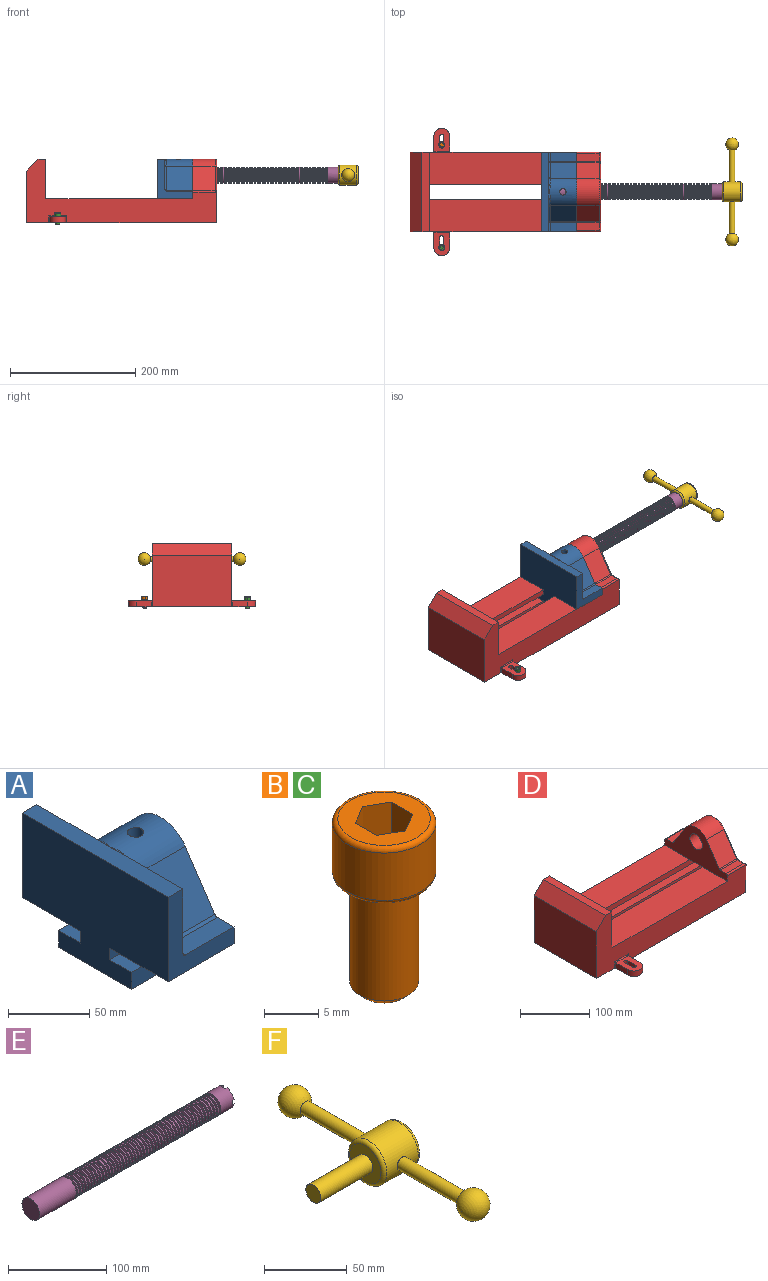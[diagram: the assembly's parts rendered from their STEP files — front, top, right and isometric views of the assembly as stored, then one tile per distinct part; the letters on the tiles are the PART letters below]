
ASSEMBLY  parts=6 mates=6
PART A: 36 faces, bbox 57.2x127x89 mm
  f0: plane 57.15x50.8mm, normal (0,0,-1), area 2903.2mm2, adj f6,f9,f10,f23
  f1: cylinder r=12.7mm len=44.45mm, axis (1,0,0), area 3464.3mm2, adj f6,f15,f16
  f2: plane 41.91x14.52mm, normal (0,0,1), area 608.5mm2, adj f6,f11,f24,f25
  f3: plane 51.86x48.26mm, normal (1,0,0), area 1495.7mm2, adj f8,f10,f31,f33,f35
  f4: plane 51.86x48.26mm, normal (1,0,0), area 1495.7mm2, adj f8,f11,f24,f28,f29
  f5: plane 57.15x50.8mm, normal (0,0,-1), area 2903.2mm2, adj f6,f9,f11,f22
  f6: plane 127x85.09mm, normal (1,0,0), area 5190.6mm2, adj f0,f1,f2,f5,f7,f10,f11,f12
  f7: plane 41.91x14.52mm, normal (0,0,1), area 608.5mm2, adj f6,f10,f30,f31
  f8: plane 127x12.7mm, normal (0,0,1), area 1612.9mm2, adj f3,f4,f9,f10,f11,f26,f34
  f9: plane 127x85.09mm, normal (-1,0,0), area 9096.8mm2, adj f0,f5,f8,f10,f11,f17,f18,f19
  f10: plane 63.5x57.15mm, normal (0,-1,0), area 1372.3mm2, adj f0,f3,f6,f7,f8,f9,f31
  f11: plane 63.5x57.15mm, normal (0,1,0), area 1372.3mm2, adj f2,f4,f5,f6,f8,f9,f24
  f12: plane 41.91x38.43mm, normal (0,-0.83,0.56), area 1939.2mm2, adj f6,f13,f30,f33
  f13: cylinder r=25.4mm len=44.45mm, axis (1,0,0), area 2026.5mm2, adj f6,f12,f14,f16,f26,f28,f34,f35
  f14: plane 41.91x38.43mm, normal (0,0.83,0.56), area 1939.2mm2, adj f6,f13,f25,f29
  f15: plane 25.4x25.4mm, normal (1,0,0), area 506.7mm2, adj f1
  f16: cylinder r=5.08mm len=13.76mm, axis (0,0,1), area 414mm2, adj f1,f13
  f17: plane 57.15x19.05mm, normal (0,0,1), area 1088.7mm2, adj f6,f9,f18,f23
  f18: plane 57.15x12.7mm, normal (0,-1,0), area 725.8mm2, adj f6,f9,f17,f19
  f19: plane 63.5x57.15mm, normal (0,0,-1), area 3629mm2, adj f6,f9,f18,f20
  f20: plane 57.15x12.7mm, normal (0,1,0), area 725.8mm2, adj f6,f9,f19,f21
  f21: plane 57.15x19.05mm, normal (0,0,1), area 1088.7mm2, adj f6,f9,f20,f22
  f22: plane 57.15x8.89mm, normal (0,1,0), area 508.1mm2, adj f5,f6,f9,f21
  f23: plane 57.15x8.89mm, normal (0,-1,0), area 508.1mm2, adj f0,f6,f9,f17
  f24: cylinder r=2.54mm len=14.52mm, axis (0,-1,0), area 57.9mm2, adj f2,f4,f11,f27
  f25: cylinder r=2.54mm len=41.91mm, axis (1,0,0), area 104.3mm2, adj f2,f6,f14,f27
  f26: bspline ~12.24x2.8mm, area 20.9mm2, adj f8,f13,f28
  f27: sphere r=2.54mm, area 6.3mm2, adj f24,f25,f29
  f28: torus R=27.94mm, axis (1,0,0), area 57.8mm2, adj f4,f13,f26,f29
  f29: cylinder r=2.54mm len=39.84mm, axis (0,-0.56,0.83), area 184.6mm2, adj f4,f14,f27,f28
  f30: cylinder r=2.54mm len=41.91mm, axis (1,0,0), area 104.3mm2, adj f6,f7,f12,f32
  f31: cylinder r=2.54mm len=14.52mm, axis (0,-1,0), area 57.9mm2, adj f3,f7,f10,f32
  f32: sphere r=2.54mm, area 6.3mm2, adj f30,f31,f33
  f33: cylinder r=2.54mm len=39.84mm, axis (0,-0.56,-0.83), area 184.6mm2, adj f3,f12,f32,f35
  f34: bspline ~12.24x2.8mm, area 20.9mm2, adj f8,f13,f35
  f35: torus R=27.94mm, axis (1,0,0), area 57.8mm2, adj f3,f13,f33,f34
PART B: 15 faces, bbox 10.3x10.3x19.1 mm
  f0: plane 8.51x8.51mm, normal (0,0,1), area 37.2mm2, adj f5,f6,f7,f8,f9,f10,f14
  f1: cylinder r=3.17mm len=11.94mm, axis (0,0,1), area 238.2mm2, adj f4,f12
  f2: plane 4.83x4.83mm, normal (0,0,-1), area 18.3mm2, adj f12
  f3: cylinder r=4.76mm len=9.53mm, axis (0,0,-1), area 159.6mm2, adj f13,f14
  f4: plane 8.51x8.51mm, normal (0,0,-1), area 25.2mm2, adj f1,f13
  f5: plane 4.83x2.38mm, normal (-0.5,-0.87,0), area 13.3mm2, adj f0,f6,f10,f11
  f6: plane 4.83x2.38mm, normal (0.5,-0.87,0), area 13.3mm2, adj f0,f5,f7,f11
  f7: plane 4.83x2.75mm, normal (1,0,0), area 13.3mm2, adj f0,f6,f8,f11
  f8: plane 4.83x2.38mm, normal (0.5,0.87,0), area 13.3mm2, adj f0,f7,f9,f11
  f9: plane 4.83x2.38mm, normal (-0.5,0.87,0), area 13.3mm2, adj f0,f8,f10,f11
  f10: plane 4.83x2.75mm, normal (-1,0,0), area 13.3mm2, adj f0,f5,f9,f11
  f11: plane 5.5x4.76mm, normal (0,0,1), area 19.6mm2, adj f5,f6,f7,f8,f9,f10
  f12: cone r=3.17mm half-angle=45deg, axis (0,0,1), area 18.9mm2, adj f1,f2
  f13: torus R=4.25mm, axis (0,0,1), area 23mm2, adj f3,f4
  f14: torus R=4.25mm, axis (0,0,1), area 23mm2, adj f0,f3
PART C: same geometry as B
PART D: 61 faces, bbox 304.8x203.2x103.7 mm
  f0: plane 304.8x101.6mm, normal (0,1,0), area 13520.3mm2, adj f3,f4,f5,f6,f7,f8,f9,f16
  f1: plane 304.8x101.6mm, normal (0,-1,0), area 13520.3mm2, adj f2,f3,f5,f6,f7,f8,f9,f16
  f2: plane 234.95x50.8mm, normal (0,0,1), area 11935.5mm2, adj f1,f5,f16,f26
  f3: plane 127x99.06mm, normal (1,0,0), area 7097.5mm2, adj f0,f1,f9,f14,f17,f18,f19,f20
  f4: plane 234.95x50.8mm, normal (0,0,1), area 11935.5mm2, adj f0,f5,f16,f27
  f5: plane 127x101.6mm, normal (1,0,0), area 9516.1mm2, adj f0,f1,f2,f4,f6,f9,f18,f19
  f6: plane 127x12.7mm, normal (0,0,1), area 1612.9mm2, adj f0,f1,f5,f7
  f7: plane 127x19.05mm, normal (-0.71,0,0.71), area 3421.5mm2, adj f0,f1,f6,f8
  f8: plane 127x82.55mm, normal (-1,0,0), area 10483.8mm2, adj f0,f1,f7,f9
  f9: plane 304.8x203.2mm, normal (0,0,-1), area 33298.3mm2, adj f0,f1,f3,f5,f8,f21,f22,f39
  f10: plane 35.56x11.98mm, normal (0,0,1), area 426mm2, adj f16,f28,f29,f30
  f11: plane 38.43x35.56mm, normal (0,0.83,0.56), area 1645.4mm2, adj f12,f16,f29,f32
  f12: cylinder r=25.4mm len=42.19mm, axis (1,0,0), area 1770.2mm2, adj f11,f13,f16,f33
  f13: plane 38.43x35.56mm, normal (0,-0.83,0.56), area 1645.4mm2, adj f12,f16,f34,f35
  f14: cylinder r=12.7mm len=38.1mm, axis (1,0,0), area 3040.2mm2, adj f3,f16
  f15: plane 35.56x11.98mm, normal (0,0,1), area 426mm2, adj f16,f34,f36,f38
  f16: plane 127x63.5mm, normal (-1,0,0), area 4155.5mm2, adj f0,f1,f2,f4,f10,f11,f12,f13
  f17: plane 38.1x25.4mm, normal (0,0,-1), area 967.7mm2, adj f3,f16,f26,f27
  f18: plane 273.05x19.05mm, normal (0,0,-1), area 5201.6mm2, adj f3,f5,f19,f26
  f19: plane 273.05x12.7mm, normal (0,1,0), area 3467.7mm2, adj f3,f5,f18,f20
  f20: plane 273.05x19.05mm, normal (0,0,1), area 5201.6mm2, adj f3,f5,f19,f21
  f21: plane 273.05x16.51mm, normal (0,1,0), area 4508.1mm2, adj f3,f5,f9,f20
  f22: plane 273.05x16.51mm, normal (0,-1,0), area 4508.1mm2, adj f3,f5,f9,f23
  f23: plane 273.05x19.05mm, normal (0,0,1), area 5201.6mm2, adj f3,f5,f22,f24
  f24: plane 273.05x12.7mm, normal (0,-1,0), area 3467.7mm2, adj f3,f5,f23,f25
  f25: plane 273.05x19.05mm, normal (0,0,-1), area 5201.6mm2, adj f3,f5,f24,f27
  f26: plane 273.05x8.89mm, normal (0,1,0), area 2427.4mm2, adj f2,f3,f5,f17,f18
  f27: plane 273.05x8.89mm, normal (0,-1,0), area 2427.4mm2, adj f3,f4,f5,f17,f25
  f28: cylinder r=2.54mm len=38.1mm, axis (1,0,0), area 148.3mm2, adj f0,f10,f16,f30
  f29: cylinder r=2.54mm len=35.56mm, axis (-1,0,0), area 88.5mm2, adj f10,f11,f16,f31
  f30: cylinder r=2.54mm len=14.52mm, axis (0,1,0), area 54.3mm2, adj f3,f10,f28,f31
  f31: torus R=5.08mm, axis (-1,0,0), area 13.5mm2, adj f3,f29,f30,f32
  f32: cylinder r=2.54mm len=39.84mm, axis (0,0.56,-0.83), area 184.6mm2, adj f3,f11,f31,f33
  f33: torus R=22.86mm, axis (-1,0,0), area 191.4mm2, adj f3,f12,f32,f35
  f34: cylinder r=2.54mm len=35.56mm, axis (-1,0,0), area 88.5mm2, adj f13,f15,f16,f37
  f35: cylinder r=2.54mm len=39.84mm, axis (0,0.56,0.83), area 184.6mm2, adj f3,f13,f33,f37
  f36: cylinder r=2.54mm len=38.1mm, axis (-1,0,0), area 148.3mm2, adj f1,f15,f16,f38
  f37: torus R=5.08mm, axis (-1,0,0), area 13.5mm2, adj f3,f34,f35,f38
  f38: cylinder r=2.54mm len=14.52mm, axis (0,1,0), area 54.3mm2, adj f3,f15,f36,f37
  f39: plane 23.88x9.53mm, normal (-1,0,0), area 227.4mm2, adj f9,f45,f46,f60
  f40: plane 23.88x9.53mm, normal (1,0,0), area 227.4mm2, adj f9,f45,f46,f58
  f41: cylinder r=3.3mm len=9.53mm, axis (0,0,-1), area 98.8mm2, adj f9,f42,f44,f46
  f42: plane 15.62x9.53mm, normal (-1,0,0), area 148.8mm2, adj f9,f41,f43,f46
  f43: cylinder r=3.3mm len=9.53mm, axis (0,0,-1), area 98.8mm2, adj f9,f42,f44,f46
  f44: plane 15.62x9.53mm, normal (1,0,0), area 148.8mm2, adj f9,f41,f43,f46
  f45: cylinder r=12.7mm len=25.4mm, axis (0,0,-1), area 380mm2, adj f9,f39,f40,f46
  f46: plane 36.58x25.4mm, normal (0,0,1), area 722.4mm2, adj f39,f40,f41,f42,f43,f44,f45,f59
  f47: plane 23.88x9.53mm, normal (-1,0,0), area 227.4mm2, adj f9,f53,f54,f56
  f48: plane 23.88x9.53mm, normal (1,0,0), area 227.4mm2, adj f9,f53,f54,f55
  f49: cylinder r=3.3mm len=9.53mm, axis (0,0,-1), area 98.8mm2, adj f9,f50,f52,f54
  f50: plane 15.62x9.53mm, normal (-1,0,0), area 148.8mm2, adj f9,f49,f51,f54
  f51: cylinder r=3.3mm len=9.53mm, axis (0,0,-1), area 98.8mm2, adj f9,f50,f52,f54
  f52: plane 15.62x9.53mm, normal (1,0,0), area 148.8mm2, adj f9,f49,f51,f54
  f53: cylinder r=12.7mm len=25.4mm, axis (0,0,-1), area 380mm2, adj f9,f47,f48,f54
  f54: plane 36.58x25.4mm, normal (0,0,1), area 722.4mm2, adj f47,f48,f49,f50,f51,f52,f53,f57
  f55: cylinder r=1.52mm len=11.05mm, axis (0,0,-1), area 24.1mm2, adj f0,f9,f48,f57
  f56: cylinder r=1.52mm len=11.05mm, axis (0,0,1), area 24.1mm2, adj f0,f9,f47,f57
  f57: cylinder r=1.52mm len=28.45mm, axis (1,0,0), area 63.5mm2, adj f0,f54,f55,f56
  f58: cylinder r=1.52mm len=11.05mm, axis (0,0,1), area 24.1mm2, adj f1,f9,f40,f59
  f59: cylinder r=1.52mm len=28.45mm, axis (-1,0,0), area 63.5mm2, adj f1,f46,f58,f60
  f60: cylinder r=1.52mm len=11.05mm, axis (0,0,-1), area 24.1mm2, adj f1,f9,f39,f59
PART E: 220 faces, bbox 279.4x25.4x25.4 mm
  f0: cylinder r=12.7mm len=25.4mm, axis (-1,0,0), area 1468.2mm2, adj f1,f2,f3,f5,f7,f208,f209,f210
  f1: plane 9.9x9.9mm, normal (1,0,0), area 62.3mm2, adj f0,f4,f213,f216
  f2: plane 9.9x9.9mm, normal (1,0,0), area 62.3mm2, adj f0,f4,f210,f218
  f3: plane 9.9x9.9mm, normal (1,0,0), area 62.3mm2, adj f0,f4,f209,f212
  f4: cylinder r=6.35mm len=25.4mm, axis (1,0,0), area 960.3mm2, adj f1,f2,f3,f5,f6,f208,f209,f210
  f5: plane 9.9x9.9mm, normal (1,0,0), area 62.3mm2, adj f0,f4,f215,f217
  f6: plane 12.7x12.7mm, normal (1,0,0), area 126.7mm2, adj f4
  f7: cone r=12.7mm half-angle=76deg, axis (1,0,0), area 188mm2, adj f0,f9
  f8: cone r=10.16mm half-angle=76deg, axis (-1,0,0), area 188mm2, adj f9,f10
  f9: cylinder r=10.16mm len=20.32mm, axis (1,0,0), area 81.1mm2, adj f7,f8
  f10: cylinder r=12.7mm len=25.4mm, axis (-1,0,0), area 131.7mm2, adj f8,f11
  f11: cone r=12.7mm half-angle=76deg, axis (1,0,0), area 188mm2, adj f10,f13
  f12: cone r=10.16mm half-angle=76deg, axis (-1,0,0), area 188mm2, adj f13,f14
  f13: cylinder r=10.16mm len=20.32mm, axis (1,0,0), area 81.1mm2, adj f11,f12
  f14: cylinder r=12.7mm len=25.4mm, axis (-1,0,0), area 131.7mm2, adj f12,f15
  f15: cone r=12.7mm half-angle=76deg, axis (1,0,0), area 188mm2, adj f14,f17
  f16: cone r=10.16mm half-angle=76deg, axis (-1,0,0), area 188mm2, adj f17,f18
  f17: cylinder r=10.16mm len=20.32mm, axis (1,0,0), area 81.1mm2, adj f15,f16
  f18: cylinder r=12.7mm len=25.4mm, axis (-1,0,0), area 131.7mm2, adj f16,f19
  f19: cone r=12.7mm half-angle=76deg, axis (1,0,0), area 188mm2, adj f18,f21
  f20: cone r=10.16mm half-angle=76deg, axis (-1,0,0), area 188mm2, adj f21,f22
  f21: cylinder r=10.16mm len=20.32mm, axis (1,0,0), area 81.1mm2, adj f19,f20
  f22: cylinder r=12.7mm len=25.4mm, axis (-1,0,0), area 131.7mm2, adj f20,f23
  f23: cone r=12.7mm half-angle=76deg, axis (1,0,0), area 188mm2, adj f22,f25
  f24: cone r=10.16mm half-angle=76deg, axis (-1,0,0), area 188mm2, adj f25,f26
  f25: cylinder r=10.16mm len=20.32mm, axis (1,0,0), area 81.1mm2, adj f23,f24
  f26: cylinder r=12.7mm len=25.4mm, axis (-1,0,0), area 131.7mm2, adj f24,f27
  f27: cone r=12.7mm half-angle=76deg, axis (1,0,0), area 188mm2, adj f26,f29
  f28: cone r=10.16mm half-angle=76deg, axis (-1,0,0), area 188mm2, adj f29,f30
  f29: cylinder r=10.16mm len=20.32mm, axis (1,0,0), area 81.1mm2, adj f27,f28
  f30: cylinder r=12.7mm len=25.4mm, axis (-1,0,0), area 131.7mm2, adj f28,f31
  f31: cone r=12.7mm half-angle=76deg, axis (1,0,0), area 188mm2, adj f30,f33
  f32: cone r=10.16mm half-angle=76deg, axis (-1,0,0), area 188mm2, adj f33,f34
  f33: cylinder r=10.16mm len=20.32mm, axis (1,0,0), area 81.1mm2, adj f31,f32
  f34: cylinder r=12.7mm len=25.4mm, axis (-1,0,0), area 131.7mm2, adj f32,f35
  f35: cone r=12.7mm half-angle=76deg, axis (1,0,0), area 188mm2, adj f34,f37
  f36: cone r=10.16mm half-angle=76deg, axis (-1,0,0), area 188mm2, adj f37,f38
  f37: cylinder r=10.16mm len=20.32mm, axis (1,0,0), area 81.1mm2, adj f35,f36
  f38: cylinder r=12.7mm len=25.4mm, axis (-1,0,0), area 131.7mm2, adj f36,f39
  f39: cone r=12.7mm half-angle=76deg, axis (1,0,0), area 188mm2, adj f38,f41
  f40: cone r=10.16mm half-angle=76deg, axis (-1,0,0), area 188mm2, adj f41,f42
  f41: cylinder r=10.16mm len=20.32mm, axis (1,0,0), area 81.1mm2, adj f39,f40
  f42: cylinder r=12.7mm len=25.4mm, axis (-1,0,0), area 131.7mm2, adj f40,f43
  f43: cone r=12.7mm half-angle=76deg, axis (1,0,0), area 188mm2, adj f42,f45
  f44: cone r=10.16mm half-angle=76deg, axis (-1,0,0), area 188mm2, adj f45,f46
  f45: cylinder r=10.16mm len=20.32mm, axis (1,0,0), area 81.1mm2, adj f43,f44
  f46: cylinder r=12.7mm len=25.4mm, axis (-1,0,0), area 131.7mm2, adj f44,f47
  f47: cone r=12.7mm half-angle=76deg, axis (1,0,0), area 188mm2, adj f46,f49
  f48: cone r=10.16mm half-angle=76deg, axis (-1,0,0), area 188mm2, adj f49,f50
  f49: cylinder r=10.16mm len=20.32mm, axis (1,0,0), area 81.1mm2, adj f47,f48
  f50: cylinder r=12.7mm len=25.4mm, axis (-1,0,0), area 131.7mm2, adj f48,f51
  f51: cone r=12.7mm half-angle=76deg, axis (1,0,0), area 188mm2, adj f50,f53
  f52: cone r=10.16mm half-angle=76deg, axis (-1,0,0), area 188mm2, adj f53,f54
  f53: cylinder r=10.16mm len=20.32mm, axis (1,0,0), area 81.1mm2, adj f51,f52
  f54: cylinder r=12.7mm len=25.4mm, axis (-1,0,0), area 131.7mm2, adj f52,f55
  f55: cone r=12.7mm half-angle=76deg, axis (1,0,0), area 188mm2, adj f54,f57
  f56: cone r=10.16mm half-angle=76deg, axis (-1,0,0), area 188mm2, adj f57,f58
  f57: cylinder r=10.16mm len=20.32mm, axis (1,0,0), area 81.1mm2, adj f55,f56
  f58: cylinder r=12.7mm len=25.4mm, axis (-1,0,0), area 131.7mm2, adj f56,f59
  f59: cone r=12.7mm half-angle=76deg, axis (1,0,0), area 188mm2, adj f58,f61
  f60: cone r=10.16mm half-angle=76deg, axis (-1,0,0), area 188mm2, adj f61,f62
  f61: cylinder r=10.16mm len=20.32mm, axis (1,0,0), area 81.1mm2, adj f59,f60
  f62: cylinder r=12.7mm len=25.4mm, axis (-1,0,0), area 131.7mm2, adj f60,f63
  f63: cone r=12.7mm half-angle=76deg, axis (1,0,0), area 188mm2, adj f62,f65
  f64: cone r=10.16mm half-angle=76deg, axis (-1,0,0), area 188mm2, adj f65,f66
  f65: cylinder r=10.16mm len=20.32mm, axis (1,0,0), area 81.1mm2, adj f63,f64
  f66: cylinder r=12.7mm len=25.4mm, axis (-1,0,0), area 131.7mm2, adj f64,f67
  f67: cone r=12.7mm half-angle=76deg, axis (1,0,0), area 188mm2, adj f66,f69
  f68: cone r=10.16mm half-angle=76deg, axis (-1,0,0), area 188mm2, adj f69,f70
  f69: cylinder r=10.16mm len=20.32mm, axis (1,0,0), area 81.1mm2, adj f67,f68
  f70: cylinder r=12.7mm len=25.4mm, axis (-1,0,0), area 131.7mm2, adj f68,f71
  f71: cone r=12.7mm half-angle=76deg, axis (1,0,0), area 188mm2, adj f70,f73
  f72: cone r=10.16mm half-angle=76deg, axis (-1,0,0), area 188mm2, adj f73,f74
  f73: cylinder r=10.16mm len=20.32mm, axis (1,0,0), area 81.1mm2, adj f71,f72
  f74: cylinder r=12.7mm len=25.4mm, axis (-1,0,0), area 131.7mm2, adj f72,f75
  f75: cone r=12.7mm half-angle=76deg, axis (1,0,0), area 188mm2, adj f74,f77
  f76: cone r=10.16mm half-angle=76deg, axis (-1,0,0), area 188mm2, adj f77,f78
  f77: cylinder r=10.16mm len=20.32mm, axis (1,0,0), area 81.1mm2, adj f75,f76
  f78: cylinder r=12.7mm len=25.4mm, axis (-1,0,0), area 131.7mm2, adj f76,f79
  f79: cone r=12.7mm half-angle=76deg, axis (1,0,0), area 188mm2, adj f78,f81
  f80: cone r=10.16mm half-angle=76deg, axis (-1,0,0), area 188mm2, adj f81,f82
  f81: cylinder r=10.16mm len=20.32mm, axis (1,0,0), area 81.1mm2, adj f79,f80
  f82: cylinder r=12.7mm len=25.4mm, axis (-1,0,0), area 131.7mm2, adj f80,f83
  f83: cone r=12.7mm half-angle=76deg, axis (1,0,0), area 188mm2, adj f82,f85
  f84: cone r=10.16mm half-angle=76deg, axis (-1,0,0), area 188mm2, adj f85,f86
  f85: cylinder r=10.16mm len=20.32mm, axis (1,0,0), area 81.1mm2, adj f83,f84
  f86: cylinder r=12.7mm len=25.4mm, axis (-1,0,0), area 131.7mm2, adj f84,f87
  f87: cone r=12.7mm half-angle=76deg, axis (1,0,0), area 188mm2, adj f86,f89
  f88: cone r=10.16mm half-angle=76deg, axis (-1,0,0), area 188mm2, adj f89,f90
  f89: cylinder r=10.16mm len=20.32mm, axis (1,0,0), area 81.1mm2, adj f87,f88
  f90: cylinder r=12.7mm len=25.4mm, axis (-1,0,0), area 131.7mm2, adj f88,f91
  f91: cone r=12.7mm half-angle=76deg, axis (1,0,0), area 188mm2, adj f90,f93
  f92: cone r=10.16mm half-angle=76deg, axis (-1,0,0), area 188mm2, adj f93,f94
  f93: cylinder r=10.16mm len=20.32mm, axis (1,0,0), area 81.1mm2, adj f91,f92
  f94: cylinder r=12.7mm len=25.4mm, axis (-1,0,0), area 131.7mm2, adj f92,f95
  f95: cone r=12.7mm half-angle=76deg, axis (1,0,0), area 188mm2, adj f94,f97
  f96: cone r=10.16mm half-angle=76deg, axis (-1,0,0), area 188mm2, adj f97,f98
  f97: cylinder r=10.16mm len=20.32mm, axis (1,0,0), area 81.1mm2, adj f95,f96
  f98: cylinder r=12.7mm len=25.4mm, axis (-1,0,0), area 131.7mm2, adj f96,f99
  f99: cone r=12.7mm half-angle=76deg, axis (1,0,0), area 188mm2, adj f98,f101
  f100: cone r=10.16mm half-angle=76deg, axis (-1,0,0), area 188mm2, adj f101,f102
  f101: cylinder r=10.16mm len=20.32mm, axis (1,0,0), area 81.1mm2, adj f99,f100
  f102: cylinder r=12.7mm len=25.4mm, axis (-1,0,0), area 131.7mm2, adj f100,f103
  f103: cone r=12.7mm half-angle=76deg, axis (1,0,0), area 188mm2, adj f102,f105
  f104: cone r=10.16mm half-angle=76deg, axis (-1,0,0), area 188mm2, adj f105,f106
  f105: cylinder r=10.16mm len=20.32mm, axis (1,0,0), area 81.1mm2, adj f103,f104
  f106: cylinder r=12.7mm len=25.4mm, axis (-1,0,0), area 131.7mm2, adj f104,f107
  f107: cone r=12.7mm half-angle=76deg, axis (1,0,0), area 188mm2, adj f106,f109
  f108: cone r=10.16mm half-angle=76deg, axis (-1,0,0), area 188mm2, adj f109,f110
  f109: cylinder r=10.16mm len=20.32mm, axis (1,0,0), area 81.1mm2, adj f107,f108
  f110: cylinder r=12.7mm len=25.4mm, axis (-1,0,0), area 131.7mm2, adj f108,f111
  f111: cone r=12.7mm half-angle=76deg, axis (1,0,0), area 188mm2, adj f110,f113
  f112: cone r=10.16mm half-angle=76deg, axis (-1,0,0), area 188mm2, adj f113,f114
  f113: cylinder r=10.16mm len=20.32mm, axis (1,0,0), area 81.1mm2, adj f111,f112
  f114: cylinder r=12.7mm len=25.4mm, axis (-1,0,0), area 131.7mm2, adj f112,f115
  f115: cone r=12.7mm half-angle=76deg, axis (1,0,0), area 188mm2, adj f114,f117
  f116: cone r=10.16mm half-angle=76deg, axis (-1,0,0), area 188mm2, adj f117,f118
  f117: cylinder r=10.16mm len=20.32mm, axis (1,0,0), area 81.1mm2, adj f115,f116
  f118: cylinder r=12.7mm len=25.4mm, axis (-1,0,0), area 131.7mm2, adj f116,f119
  f119: cone r=12.7mm half-angle=76deg, axis (1,0,0), area 188mm2, adj f118,f121
  f120: cone r=10.16mm half-angle=76deg, axis (-1,0,0), area 188mm2, adj f121,f122
  f121: cylinder r=10.16mm len=20.32mm, axis (1,0,0), area 81.1mm2, adj f119,f120
  f122: cylinder r=12.7mm len=25.4mm, axis (-1,0,0), area 131.7mm2, adj f120,f123
  f123: cone r=12.7mm half-angle=76deg, axis (1,0,0), area 188mm2, adj f122,f125
  f124: cone r=10.16mm half-angle=76deg, axis (-1,0,0), area 188mm2, adj f125,f126
  f125: cylinder r=10.16mm len=20.32mm, axis (1,0,0), area 81.1mm2, adj f123,f124
  f126: cylinder r=12.7mm len=25.4mm, axis (-1,0,0), area 131.7mm2, adj f124,f127
  f127: cone r=12.7mm half-angle=76deg, axis (1,0,0), area 188mm2, adj f126,f129
  f128: cone r=10.16mm half-angle=76deg, axis (-1,0,0), area 188mm2, adj f129,f130
  f129: cylinder r=10.16mm len=20.32mm, axis (1,0,0), area 81.1mm2, adj f127,f128
  f130: cylinder r=12.7mm len=25.4mm, axis (-1,0,0), area 131.7mm2, adj f128,f131
  f131: cone r=12.7mm half-angle=76deg, axis (1,0,0), area 188mm2, adj f130,f133
  f132: cone r=10.16mm half-angle=76deg, axis (-1,0,0), area 188mm2, adj f133,f134
  f133: cylinder r=10.16mm len=20.32mm, axis (1,0,0), area 81.1mm2, adj f131,f132
  f134: cylinder r=12.7mm len=25.4mm, axis (-1,0,0), area 131.7mm2, adj f132,f135
  f135: cone r=12.7mm half-angle=76deg, axis (1,0,0), area 188mm2, adj f134,f137
  f136: cone r=10.16mm half-angle=76deg, axis (-1,0,0), area 188mm2, adj f137,f138
  f137: cylinder r=10.16mm len=20.32mm, axis (1,0,0), area 81.1mm2, adj f135,f136
  f138: cylinder r=12.7mm len=25.4mm, axis (-1,0,0), area 131.7mm2, adj f136,f139
  f139: cone r=12.7mm half-angle=76deg, axis (1,0,0), area 188mm2, adj f138,f141
  f140: cone r=10.16mm half-angle=76deg, axis (-1,0,0), area 188mm2, adj f141,f142
  f141: cylinder r=10.16mm len=20.32mm, axis (1,0,0), area 81.1mm2, adj f139,f140
  f142: cylinder r=12.7mm len=25.4mm, axis (-1,0,0), area 131.7mm2, adj f140,f143
  f143: cone r=12.7mm half-angle=76deg, axis (1,0,0), area 188mm2, adj f142,f145
  f144: cone r=10.16mm half-angle=76deg, axis (-1,0,0), area 188mm2, adj f145,f146
  f145: cylinder r=10.16mm len=20.32mm, axis (1,0,0), area 81.1mm2, adj f143,f144
  f146: cylinder r=12.7mm len=25.4mm, axis (-1,0,0), area 131.7mm2, adj f144,f147
  f147: cone r=12.7mm half-angle=76deg, axis (1,0,0), area 188mm2, adj f146,f149
  f148: cone r=10.16mm half-angle=76deg, axis (-1,0,0), area 188mm2, adj f149,f150
  f149: cylinder r=10.16mm len=20.32mm, axis (1,0,0), area 81.1mm2, adj f147,f148
  f150: cylinder r=12.7mm len=25.4mm, axis (-1,0,0), area 131.7mm2, adj f148,f151
  f151: cone r=12.7mm half-angle=76deg, axis (1,0,0), area 188mm2, adj f150,f153
  f152: cone r=10.16mm half-angle=76deg, axis (-1,0,0), area 188mm2, adj f153,f154
  f153: cylinder r=10.16mm len=20.32mm, axis (1,0,0), area 81.1mm2, adj f151,f152
  f154: cylinder r=12.7mm len=25.4mm, axis (-1,0,0), area 131.7mm2, adj f152,f155
  f155: cone r=12.7mm half-angle=76deg, axis (1,0,0), area 188mm2, adj f154,f157
  f156: cone r=10.16mm half-angle=76deg, axis (-1,0,0), area 188mm2, adj f157,f158
  f157: cylinder r=10.16mm len=20.32mm, axis (1,0,0), area 81.1mm2, adj f155,f156
  f158: cylinder r=12.7mm len=25.4mm, axis (-1,0,0), area 131.7mm2, adj f156,f159
  f159: cone r=12.7mm half-angle=76deg, axis (1,0,0), area 188mm2, adj f158,f161
  f160: cone r=10.16mm half-angle=76deg, axis (-1,0,0), area 188mm2, adj f161,f162
  f161: cylinder r=10.16mm len=20.32mm, axis (1,0,0), area 81.1mm2, adj f159,f160
  f162: cylinder r=12.7mm len=25.4mm, axis (-1,0,0), area 131.7mm2, adj f160,f163
  f163: cone r=12.7mm half-angle=76deg, axis (1,0,0), area 188mm2, adj f162,f165
  f164: cone r=10.16mm half-angle=76deg, axis (-1,0,0), area 188mm2, adj f165,f166
  f165: cylinder r=10.16mm len=20.32mm, axis (1,0,0), area 81.1mm2, adj f163,f164
  f166: cylinder r=12.7mm len=25.4mm, axis (-1,0,0), area 131.7mm2, adj f164,f167
  f167: cone r=12.7mm half-angle=76deg, axis (1,0,0), area 188mm2, adj f166,f169
  f168: cone r=10.16mm half-angle=76deg, axis (-1,0,0), area 188mm2, adj f169,f170
  f169: cylinder r=10.16mm len=20.32mm, axis (1,0,0), area 81.1mm2, adj f167,f168
  f170: cylinder r=12.7mm len=25.4mm, axis (-1,0,0), area 131.7mm2, adj f168,f171
  f171: cone r=12.7mm half-angle=76deg, axis (1,0,0), area 188mm2, adj f170,f173
  f172: cone r=10.16mm half-angle=76deg, axis (-1,0,0), area 188mm2, adj f173,f174
  f173: cylinder r=10.16mm len=20.32mm, axis (1,0,0), area 81.1mm2, adj f171,f172
  f174: cylinder r=12.7mm len=25.4mm, axis (-1,0,0), area 131.7mm2, adj f172,f175
  f175: cone r=12.7mm half-angle=76deg, axis (1,0,0), area 188mm2, adj f174,f177
  f176: cone r=10.16mm half-angle=76deg, axis (-1,0,0), area 188mm2, adj f177,f178
  f177: cylinder r=10.16mm len=20.32mm, axis (1,0,0), area 81.1mm2, adj f175,f176
  f178: cylinder r=12.7mm len=25.4mm, axis (-1,0,0), area 131.7mm2, adj f176,f179
  f179: cone r=12.7mm half-angle=76deg, axis (1,0,0), area 188mm2, adj f178,f181
  f180: cone r=10.16mm half-angle=76deg, axis (-1,0,0), area 188mm2, adj f181,f182
  f181: cylinder r=10.16mm len=20.32mm, axis (1,0,0), area 81.1mm2, adj f179,f180
  f182: cylinder r=12.7mm len=25.4mm, axis (-1,0,0), area 131.7mm2, adj f180,f183
  f183: cone r=12.7mm half-angle=76deg, axis (1,0,0), area 188mm2, adj f182,f185
  f184: cone r=10.16mm half-angle=76deg, axis (-1,0,0), area 188mm2, adj f185,f186
  f185: cylinder r=10.16mm len=20.32mm, axis (1,0,0), area 81.1mm2, adj f183,f184
  f186: cylinder r=12.7mm len=25.4mm, axis (-1,0,0), area 131.7mm2, adj f184,f187
  f187: cone r=12.7mm half-angle=76deg, axis (1,0,0), area 188mm2, adj f186,f189
  f188: cone r=10.16mm half-angle=76deg, axis (-1,0,0), area 188mm2, adj f189,f190
  f189: cylinder r=10.16mm len=20.32mm, axis (1,0,0), area 81.1mm2, adj f187,f188
  f190: cylinder r=12.7mm len=25.4mm, axis (-1,0,0), area 131.7mm2, adj f188,f191
  f191: cone r=12.7mm half-angle=76deg, axis (1,0,0), area 188mm2, adj f190,f193
  f192: cone r=10.16mm half-angle=76deg, axis (-1,0,0), area 188mm2, adj f193,f194
  f193: cylinder r=10.16mm len=20.32mm, axis (1,0,0), area 81.1mm2, adj f191,f192
  f194: cylinder r=12.7mm len=25.4mm, axis (-1,0,0), area 131.7mm2, adj f192,f195
  f195: cone r=12.7mm half-angle=76deg, axis (1,0,0), area 188mm2, adj f194,f197
  f196: cone r=10.16mm half-angle=76deg, axis (-1,0,0), area 188mm2, adj f197,f198
  f197: cylinder r=10.16mm len=20.32mm, axis (1,0,0), area 81.1mm2, adj f195,f196
  f198: cylinder r=12.7mm len=25.4mm, axis (-1,0,0), area 131.7mm2, adj f196,f199
  f199: cone r=12.7mm half-angle=76deg, axis (1,0,0), area 188mm2, adj f198,f201
  f200: cone r=10.16mm half-angle=76deg, axis (-1,0,0), area 188mm2, adj f201,f202
  f201: cylinder r=10.16mm len=20.32mm, axis (1,0,0), area 81.1mm2, adj f199,f200
  f202: cylinder r=12.7mm len=25.4mm, axis (-1,0,0), area 131.7mm2, adj f200,f203
  f203: cone r=12.7mm half-angle=76deg, axis (1,0,0), area 188mm2, adj f202,f205
  f204: cone r=10.16mm half-angle=76deg, axis (-1,0,0), area 188mm2, adj f205,f207
  f205: cylinder r=10.16mm len=20.32mm, axis (1,0,0), area 81.1mm2, adj f203,f204
  f206: plane 25.4x25.4mm, normal (-1,0,0), area 506.7mm2, adj f207
  f207: cylinder r=12.7mm len=52.45mm, axis (-1,0,0), area 4185.4mm2, adj f204,f206
  f208: plane 6.88x5.08mm, normal (1,0,0), area 32.7mm2, adj f0,f4,f209,f210
  f209: plane 6.62x2.54mm, normal (0,-1,0), area 16.8mm2, adj f0,f3,f4,f208
  f210: plane 6.62x2.54mm, normal (0,1,0), area 16.8mm2, adj f0,f2,f4,f208
  f211: plane 6.88x5.08mm, normal (1,0,0), area 32.7mm2, adj f0,f4,f212,f213
  f212: plane 6.62x2.54mm, normal (0,0,1), area 16.8mm2, adj f0,f3,f4,f211
  f213: plane 6.62x2.54mm, normal (0,0,-1), area 16.8mm2, adj f0,f1,f4,f211
  f214: plane 6.88x5.08mm, normal (1,0,0), area 32.7mm2, adj f0,f4,f215,f216
  f215: plane 6.62x2.54mm, normal (0,1,0), area 16.8mm2, adj f0,f4,f5,f214
  f216: plane 6.62x2.54mm, normal (0,-1,0), area 16.8mm2, adj f0,f1,f4,f214
  f217: plane 6.62x2.54mm, normal (0,0,-1), area 16.8mm2, adj f0,f4,f5,f219
  f218: plane 6.62x2.54mm, normal (0,0,1), area 16.8mm2, adj f0,f2,f4,f219
  f219: plane 6.88x5.08mm, normal (1,0,0), area 32.7mm2, adj f0,f4,f217,f218
PART F: 11 faces, bbox 76.2x172.7x34.4 mm
  f0: sphere r=10.16mm, area 1231.8mm2, adj f1
  f1: cylinder r=4.45mm len=51.82mm, axis (0,1,0), area 1438.5mm2, adj f0,f4
  f2: sphere r=10.16mm, area 1231.8mm2, adj f3
  f3: cylinder r=4.45mm len=51.82mm, axis (0,1,0), area 1438.5mm2, adj f2,f4
  f4: cylinder r=15.88mm len=31.75mm, axis (-1,0,0), area 2534.7mm2, adj f1,f3,f9,f10
  f5: cylinder r=6.35mm len=44.45mm, axis (-1,0,0), area 1773.5mm2, adj f6,f8
  f6: plane 12.7x12.7mm, normal (-1,0,0), area 126.7mm2, adj f5
  f7: plane 26.67x26.67mm, normal (1,0,0), area 558.6mm2, adj f10
  f8: plane 26.67x26.67mm, normal (-1,0,0), area 432mm2, adj f5,f9
  f9: torus R=13.33mm, axis (1,0,0), area 374.8mm2, adj f4,f8
  f10: torus R=13.33mm, axis (1,0,0), area 374.8mm2, adj f4,f7
PLACE A t=(177.8,0,0)mm
PLACE B rot(axis=(0,0,-1),21.5deg) t=(-254,75.42,10.73)mm
PLACE C rot(axis=(0,0,-1),23.1deg) t=(-254,-88.9,9.52)mm
PLACE D at identity fixed
PLACE E rot(axis=(1,0,0),180deg) t=(177.8,0,152.4)mm
PLACE F rot(axis=(-1,0,0),180deg) t=(156.21,0,152.4)mm
MATE fastened E.f4 <-> F.f5  axis (1,0,0) through (194.31,0,76.2)mm
MATE planar A.f0 <-> D.f2  axis (0,0,-1) through (-66.68,-38.1,38.1)mm
MATE pin_slot C.f1 <-> D.f41  axis (0,0,1) through (-254,-88.9,9.52)mm
MATE revolute E.f7 <-> A.f28  axis (-1,0,0) through (-82.55,0,76.2)mm
MATE pin_slot B.f1 <-> D.f51  axis (0,0,1) through (-254,75.42,4.76)mm
MATE cylindrical D.f12 <-> E.f7  axis (-1,0,0) through (-38.1,0,76.2)mm
